# Revit family: AISC HP Shapes-Section
name_source: partatom
category: Detail Items
revit_build: Autodesk Revit Architecture 2012 (Build: 20110210_1515)
units: mm (PartAtom-declared; Revit-internal decimal feet)

## types (11) — shared parameters
Keynote = 05 12 00.E0

## per-type parameters (varying)
| type | A | W | bf | d | k | r | tf | tw |
| HP14X117 | 0.24 SF | 117 | 1' - 2 29/32" | 1' - 2 3/16" | 0' - 1 1/2" | 0' - 0 11/16" | 0' - 0 13/16" | 0' - 0 13/16" |
| HP14X102 | 0.21 SF | 102 | 1' - 2 13/16" | 1' - 2" | 0' - 1 3/8" | 0' - 0 21/32" | 0' - 0 23/32" | 0' - 0 23/32" |
| HP14X89 | 0.18 SF | 89 | 1' - 2 11/16" | 1' - 1 13/16" | 0' - 1 5/16" | 0' - 0 11/16" | 0' - 0 5/8" | 0' - 0 5/8" |
| HP14X73 | 0.15 SF | 73 | 1' - 2 19/32" | 1' - 1 19/32" | 0' - 1 3/16" | 0' - 0 11/16" | 0' - 0 1/2" | 0' - 0 1/2" |
| HP12X84 | 0.17 SF | 84 | 1' - 0 5/16" | 1' - 0 5/16" | 0' - 1 3/8" | 0' - 0 11/16" | 0' - 0 11/16" | 0' - 0 11/16" |
| HP12X74 | 0.15 SF | 74 | 1' - 0 3/16" | 1' - 0 3/32" | 0' - 1 5/16" | 0' - 0 11/16" | 0' - 0 5/8" | 0' - 0 19/32" |
| HP12X63 | 0.13 SF | 63 | 1' - 0 3/32" | 0' - 11 29/32" | 0' - 1 1/4" | 0' - 0 3/4" | 0' - 0 1/2" | 0' - 0 1/2" |
| HP12X53 | 0.11 SF | 53 | 1' - 0" | 0' - 11 13/16" | 0' - 1 1/8" | 0' - 0 11/16" | 0' - 0 7/16" | 0' - 0 7/16" |
| HP10X57 | 0.12 SF | 57 | 0' - 10 3/16" | 0' - 10" | 0' - 1 1/4" | 0' - 0 11/16" | 0' - 0 9/16" | 0' - 0 9/16" |
| HP10X42 | 0.09 SF | 42 | 0' - 10 3/32" | 0' - 9 11/16" | 0' - 1 1/8" | 0' - 0 23/32" | 0' - 0 13/32" | 0' - 0 13/32" |
| HP8X36 | 0.07 SF | 36 | 0' - 8 5/32" | 0' - 8 1/32" | 0' - 1 1/8" | 0' - 0 11/16" | 0' - 0 7/16" | 0' - 0 7/16" |
